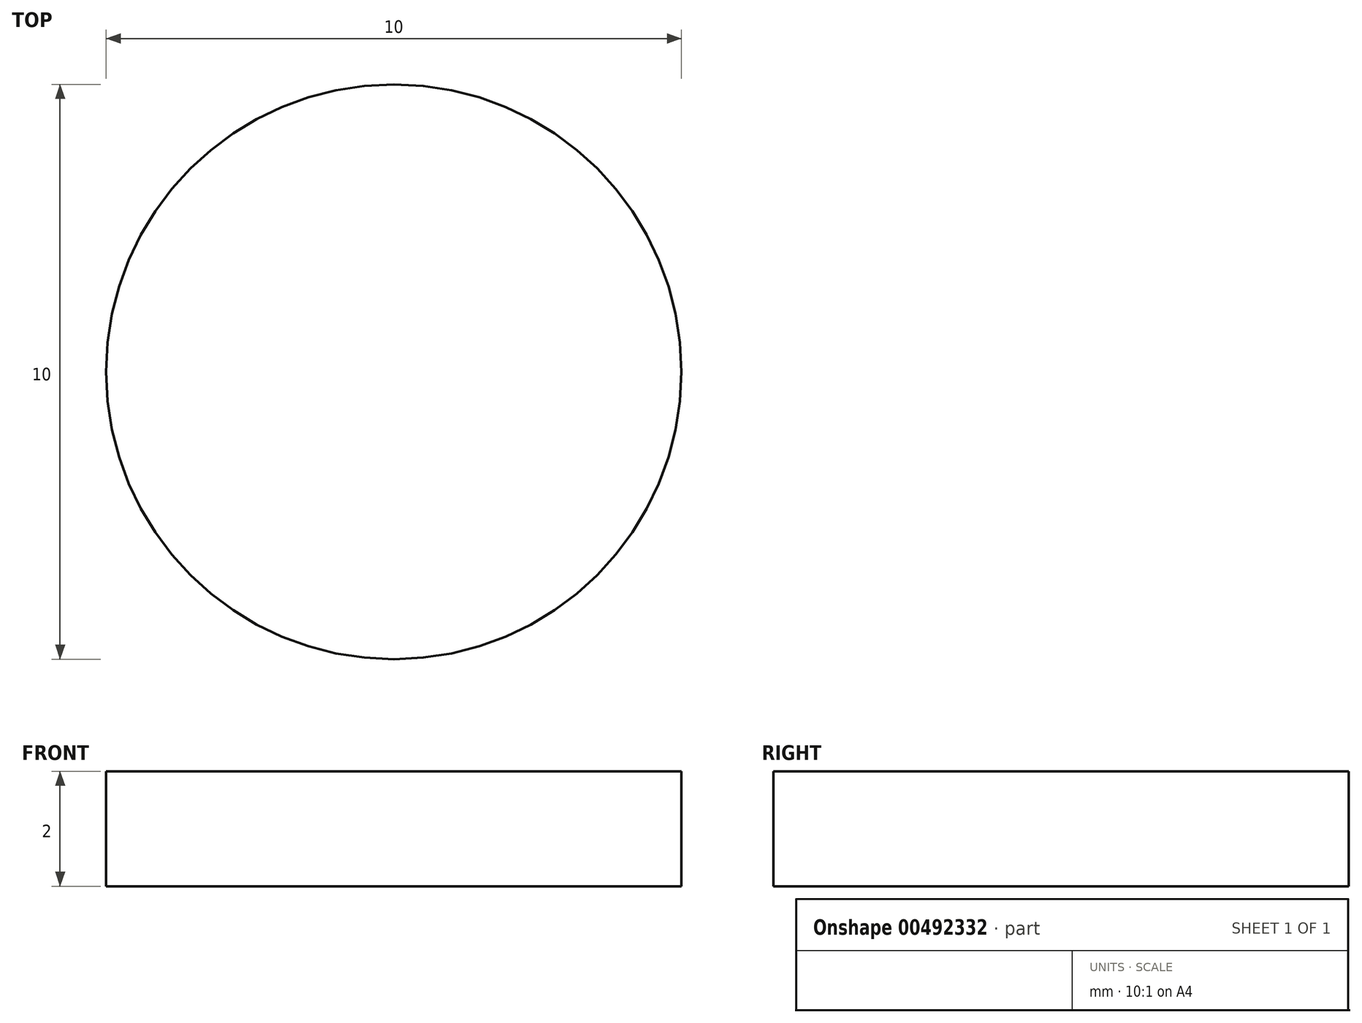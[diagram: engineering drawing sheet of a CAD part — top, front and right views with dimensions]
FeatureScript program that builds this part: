
annotation { "Feature Type Name" : "Feature", "Feature Type Description" : "" }
export const myFeature = defineFeature(function(context is Context, id is Id, definition is map)
    precondition{}
    {
        {
            var Q0;
            Q0=qCreatedBy(makeId("Top.planeOp"),FACE);
            var sketch = newSketch(context, id + "F0", { "sketchPlane" : qUnion([Q0])});
            skCircle(sketch, "E0", {"center": v(0, 0) * mm, "radius": 5 * mm});
            skSolve(sketch);
        }
        {
            var Q0;
            Q0 = qSketchRegion(id + "F0", true);
            extrude(context, id + "F1", {"entities" : qUnion([Q0]), "depth" : 2 * mm});
        }
    });
